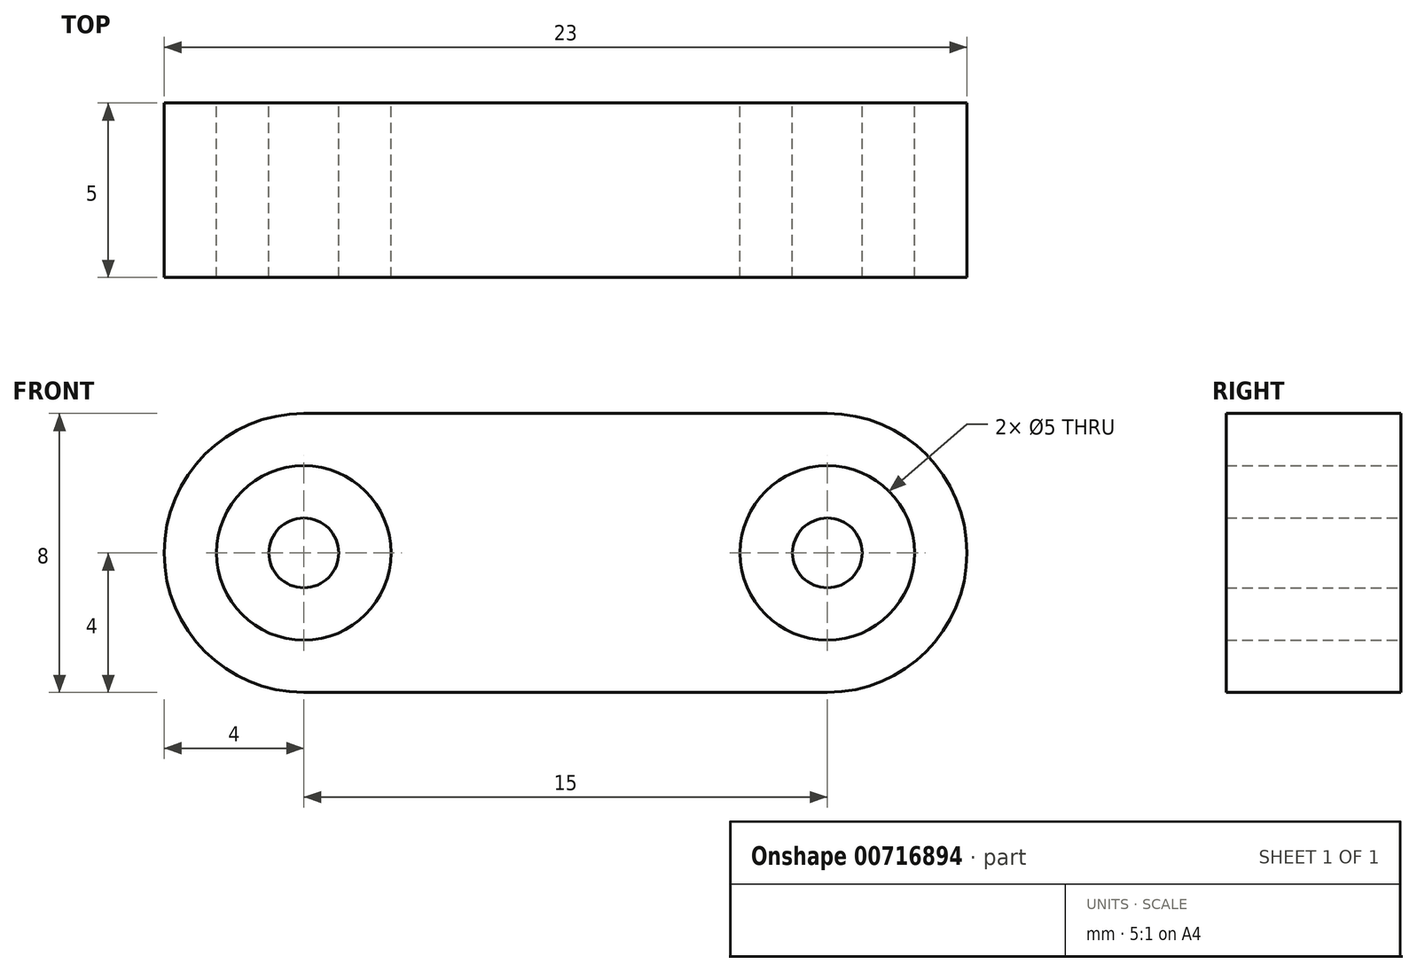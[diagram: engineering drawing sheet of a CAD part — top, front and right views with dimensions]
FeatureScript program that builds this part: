
annotation { "Feature Type Name" : "Feature", "Feature Type Description" : "" }
export const myFeature = defineFeature(function(context is Context, id is Id, definition is map)
    precondition{}
    {
        {
            var Q0;
            Q0=qCreatedBy(makeId("Front.planeOp"),FACE);
            var sketch = newSketch(context, id + "F0", { "sketchPlane" : qUnion([Q0])});
            skArc(sketch, "E0", {"start": v(0, -4) * mm, "mid": v(4, 0) * mm, "end": v(0, 4) * mm});
            skArc(sketch, "E1", {"start": v(-15, 4) * mm, "mid": v(-19, 0) * mm, "end": v(-15, -4) * mm});
            skLineSegment(sketch, "E2", {"start": v(0, 4) * mm, "end": v(-15, 4) * mm});
            skLineSegment(sketch, "E3", {"start": v(0, -4) * mm, "end": v(-15, -4) * mm});
            skCircle(sketch, "E4", {"center": v(-15, 0) * mm, "radius": 2.5 * mm});
            skCircle(sketch, "E5", {"center": v(0, 0) * mm, "radius": 2.5 * mm});
            skCircle(sketch, "E6", {"center": v(0, 0) * mm, "radius": 1 * mm});
            skCircle(sketch, "E7", {"center": v(-15, 0) * mm, "radius": 1 * mm});
            skSolve(sketch);
        }
        {
            var Q0;
            Q0 = qSketchRegion(id + "F0", true);
            var Q1;
            Q1=makeQuery(id+"F0.imprint","IMPRINT",FACE,{"disambiguationData":[TD([[makeQuery(id+"F0.imprint","IMPRINT",EDGE,{"derivedFrom":sQuery(id+"F0.wireOp",EDGE,"E7")}),1.0]])]});
            var Q2;
            Q2=makeQuery(id+"F0.imprint","IMPRINT",FACE,{"disambiguationData":[TD([[makeQuery(id+"F0.imprint","IMPRINT",EDGE,{"derivedFrom":sQuery(id+"F0.wireOp",EDGE,"E6")}),1.0]])]});
            extrude(context, id + "F1", {"entities" : qUnion([Q0, Q1, Q2]), "depth" : 5 * mm, "offsetDistance" : 25.4 * mm});
        }
    });
